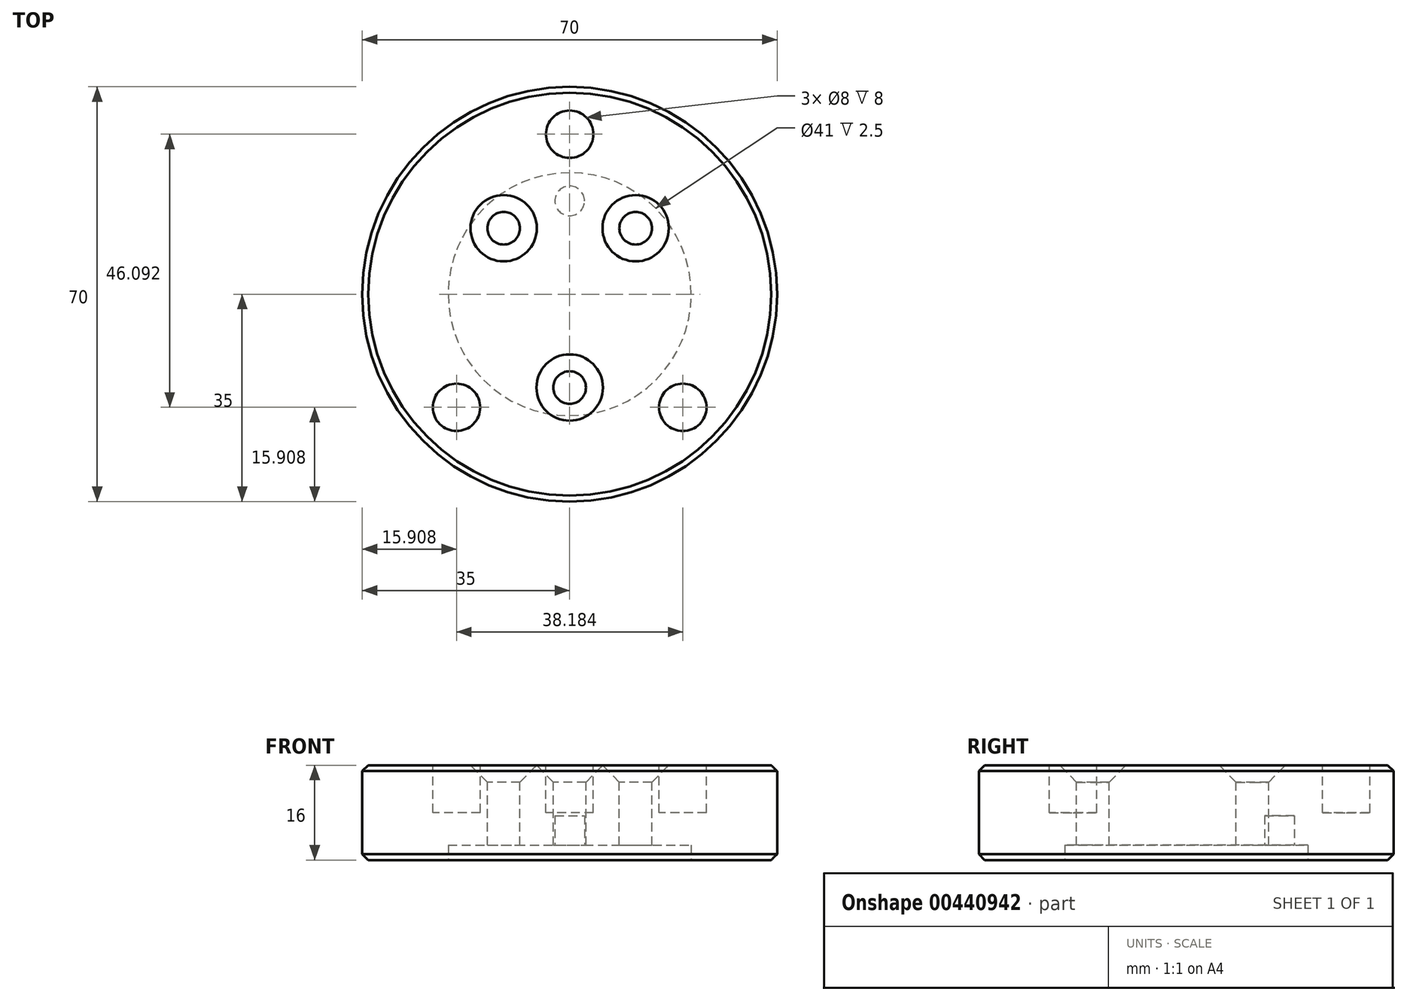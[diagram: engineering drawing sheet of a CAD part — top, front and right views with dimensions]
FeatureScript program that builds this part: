
annotation { "Feature Type Name" : "Feature", "Feature Type Description" : "" }
export const myFeature = defineFeature(function(context is Context, id is Id, definition is map)
    precondition{}
    {
        {
            var Q0;
            Q0=qCreatedBy(makeId("Top.planeOp"),FACE);
            var sketch = newSketch(context, id + "F0", { "sketchPlane" : qUnion([Q0])});
            skCircle(sketch, "E0", {"center": v(0, 0) * mm, "radius": 35 * mm});
            skSolve(sketch);
        }
        {
            var Q0;
            Q0=makeQuery(id+"F0.imprint","IMPRINT",FACE,{"disambiguationData":[TD([[makeQuery(id+"F0.imprint","IMPRINT",EDGE,{"derivedFrom":sQuery(id+"F0.wireOp",EDGE,"E0")}),1.0]])]});
            extrude(context, id + "F1", {"entities" : qUnion([Q0]), "depth" : 16 * mm});
        }
        {
            var Q0;
            Q0=makeQuery(id+"F1.opExtrude","CAP_FACE",FACE,{"disambiguationData":[OSD([sQuery(id+"F0.wireOp",EDGE,"E0")])],"isStart":true});
            var sketch = newSketch(context, id + "F2", { "sketchPlane" : qUnion([Q0])});
            skCircle(sketch, "E1", {"center": v(0, 0) * mm, "radius": 20.5 * mm});
            skSolve(sketch);
        }
        {
            var Q0;
            Q0=makeQuery(id+"F2.imprint","IMPRINT",FACE,{"disambiguationData":[TD([[makeQuery(id+"F2.imprint","IMPRINT",EDGE,{"derivedFrom":sQuery(id+"F2.wireOp",EDGE,"E1")}),1.0]])]});
            var Q1;
            Q1=sQuery(id+"F2.wireOp",EDGE,"E1");
            extrude(context, id + "F3", {"entities" : qUnion([Q0]), "operationType" : NewBodyOperationType.REMOVE, "surfaceEntities" : qUnion([Q1]), "oppositeDirection" : true, "depth" : 2.5 * mm});
        }
        {
            var Q0;
            Q0=makeQuery(id+"F1.opExtrude","CAP_FACE",FACE,{"disambiguationData":[OSD([sQuery(id+"F0.wireOp",EDGE,"E0")])],"isStart":false});
            var sketch = newSketch(context, id + "F4", { "sketchPlane" : qUnion([Q0])});
            skPoint(sketch, "E2", {"position": v(0, 0) * mm});
            skCircle(sketch, "E3", {"center": v(0, 27) * mm, "radius": 4 * mm});
            skCircle(sketch, "E4.1.0", {"center": v(-19.1, 19.1) * mm, "radius": 4 * mm});
            skCircle(sketch, "E4.2.0", {"center": v(-27, 0) * mm, "radius": 4 * mm});
            skCircle(sketch, "E4.3.0", {"center": v(-19.1, -19.1) * mm, "radius": 4 * mm});
            skCircle(sketch, "E4.4.0", {"center": v(0, -27) * mm, "radius": 4 * mm});
            skCircle(sketch, "E4.5.0", {"center": v(19.1, -19.1) * mm, "radius": 4 * mm});
            skCircle(sketch, "E4.6.0", {"center": v(27, 0) * mm, "radius": 4 * mm});
            skCircle(sketch, "E4.7.0", {"center": v(19.1, 19.1) * mm, "radius": 4 * mm});
            skPoint(sketch, "E5", {"position": v(0, 15.75) * mm});
            skPoint(sketch, "E6.1.0", {"position": v(-11.14, 11.14) * mm});
            skPoint(sketch, "E6.2.0", {"position": v(-15.75, 0) * mm});
            skPoint(sketch, "E6.3.0", {"position": v(-11.14, -11.14) * mm});
            skPoint(sketch, "E6.4.0", {"position": v(0, -15.75) * mm});
            skPoint(sketch, "E6.5.0", {"position": v(11.14, -11.14) * mm});
            skPoint(sketch, "E6.6.0", {"position": v(15.75, 0) * mm});
            skPoint(sketch, "E6.7.0", {"position": v(11.14, 11.14) * mm});
            skSolve(sketch);
        }
        {
            var Q0;
            Q0=makeQuery(id+"F4.imprint","IMPRINT",FACE,{"disambiguationData":[TD([[makeQuery(id+"F4.imprint","IMPRINT",EDGE,{"derivedFrom":sQuery(id+"F4.wireOp",EDGE,"E3")}),1.0]])]});
            var Q1;
            Q1=makeQuery(id+"F4.imprint","IMPRINT",FACE,{"disambiguationData":[TD([[makeQuery(id+"F4.imprint","IMPRINT",EDGE,{"derivedFrom":sQuery(id+"F4.wireOp",EDGE,"E4.5.0")}),1.0]])]});
            var Q2;
            Q2=makeQuery(id+"F4.imprint","IMPRINT",FACE,{"disambiguationData":[TD([[makeQuery(id+"F4.imprint","IMPRINT",EDGE,{"derivedFrom":sQuery(id+"F4.wireOp",EDGE,"E4.3.0")}),1.0]])]});
            extrude(context, id + "F5", {"entities" : qUnion([Q0, Q1, Q2]), "operationType" : NewBodyOperationType.REMOVE, "oppositeDirection" : true, "depth" : 8 * mm});
        }
        {
            var Q0;
            Q0=sQuery(id+"F4.wireOp",VERTEX,"E6.1.0");
            var Q1;
            Q1=sQuery(id+"F4.wireOp",VERTEX,"E6.7.0");
            var Q2;
            Q2=sQuery(id+"F4.wireOp",VERTEX,"E6.4.0");
            var Q3;
            Q3=makeQuery(id+"F1.opExtrude","SWEPT_BODY",BODY,{"disambiguationData":[OSD([sQuery(id+"F0.wireOp",EDGE,"E0")])]});
            hole(context, id + "F6", {"style" : HoleStyle.C_SINK, "endStyle" : HoleEndStyle.THROUGH, "standardTappedOrClearance" : lookupTablePath({ "standard" : "ISO", "fit" : "Normal", "size" : "M5", "type" : "Clearance" }), "standardBlindInLast" : lookupTablePath({ "fit" : "Standard", "standard" : "ISO", "size" : "M5", "type" : "Clearance" }), "holeDiameter" : 5.5 * mm, "cSinkDiameter" : 11.2 * mm, "cSinkAngle" : 90 * degree, "isTappedThrough" : true, "tappedDepth" : 12 * mm, "tapClearance" : 3, "locations" : qUnion([Q0, Q1, Q2]), "scope" : qUnion([Q3]), "majorDiameter" : 5 * mm});
        }
        {
            var Q0;
            Q0=makeQuery(id+"F3.boolean.opBoolean","COPY",FACE,{"derivedFrom":makeQuery(id+"F3.opExtrude","CAP_FACE",FACE,{"disambiguationData":[OSD([sQuery(id+"F2.wireOp",EDGE,"E1")])],"isStart":false})});
            var sketch = newSketch(context, id + "F7", { "sketchPlane" : qUnion([Q0])});
            skPoint(sketch, "E7", {"position": v(0, -15.75) * mm});
            skPoint(sketch, "E8.1.0", {"position": v(11.14, -11.14) * mm});
            skPoint(sketch, "E8.2.0", {"position": v(15.75, 0) * mm});
            skPoint(sketch, "E8.3.0", {"position": v(11.14, 11.14) * mm});
            skPoint(sketch, "E8.4.0", {"position": v(0, 15.75) * mm});
            skPoint(sketch, "E8.5.0", {"position": v(-11.14, 11.14) * mm});
            skPoint(sketch, "E8.6.0", {"position": v(-15.75, 0) * mm});
            skPoint(sketch, "E8.7.0", {"position": v(-11.14, -11.14) * mm});
            skPoint(sketch, "E8.center", {"position": v(0, 0) * mm});
            skCircle(sketch, "E9", {"center": v(0, -15.75) * mm, "radius": 2.5 * mm});
            skSolve(sketch);
        }
        {
            var Q0;
            Q0=makeQuery(id+"F7.imprint","IMPRINT",FACE,{"disambiguationData":[TD([[makeQuery(id+"F7.imprint","IMPRINT",EDGE,{"derivedFrom":sQuery(id+"F7.wireOp",EDGE,"E9")}),1.0]])]});
            extrude(context, id + "F8", {"entities" : qUnion([Q0]), "operationType" : NewBodyOperationType.REMOVE, "oppositeDirection" : true, "depth" : 5 * mm});
        }
        {
            var Q0;
            Q0=makeQuery(id+"F3.boolean.opBoolean","COPY",EDGE,{"derivedFrom":makeQuery(id+"F3.opExtrude","CAP_EDGE",EDGE,{"disambiguationData":[OSD([sQuery(id+"F2.wireOp",EDGE,"E1")])],"isStart":true})});
            var Q1;
            Q1=makeQuery(id+"F1.opExtrude","CAP_EDGE",EDGE,{"disambiguationData":[OSD([sQuery(id+"F0.wireOp",EDGE,"E0")])],"isStart":true});
            var Q2;
            Q2=makeQuery(id+"F1.opExtrude","CAP_EDGE",EDGE,{"disambiguationData":[OSD([sQuery(id+"F0.wireOp",EDGE,"E0")])],"isStart":false});
            var Q3;
            Q3=makeQuery(id+"F5.boolean.opBoolean","COPY",EDGE,{"derivedFrom":makeQuery(id+"F5.opExtrude","CAP_EDGE",EDGE,{"disambiguationData":[OSD([sQuery(id+"F4.wireOp",EDGE,"E4.3.0")])],"isStart":true})});
            var Q4;
            Q4=makeQuery(id+"F5.boolean.opBoolean","COPY",EDGE,{"derivedFrom":makeQuery(id+"F5.opExtrude","CAP_EDGE",EDGE,{"disambiguationData":[OSD([sQuery(id+"F4.wireOp",EDGE,"E3")])],"isStart":true})});
            var Q5;
            Q5=makeQuery(id+"F5.boolean.opBoolean","COPY",EDGE,{"derivedFrom":makeQuery(id+"F5.opExtrude","CAP_EDGE",EDGE,{"disambiguationData":[OSD([sQuery(id+"F4.wireOp",EDGE,"E4.5.0")])],"isStart":true})});
            chamfer(context, id + "F9", {"entities" : qUnion([Q0, Q1, Q2, Q3, Q4, Q5]), "width" : 1 * mm, "tangentPropagation" : true});
        }
    });
